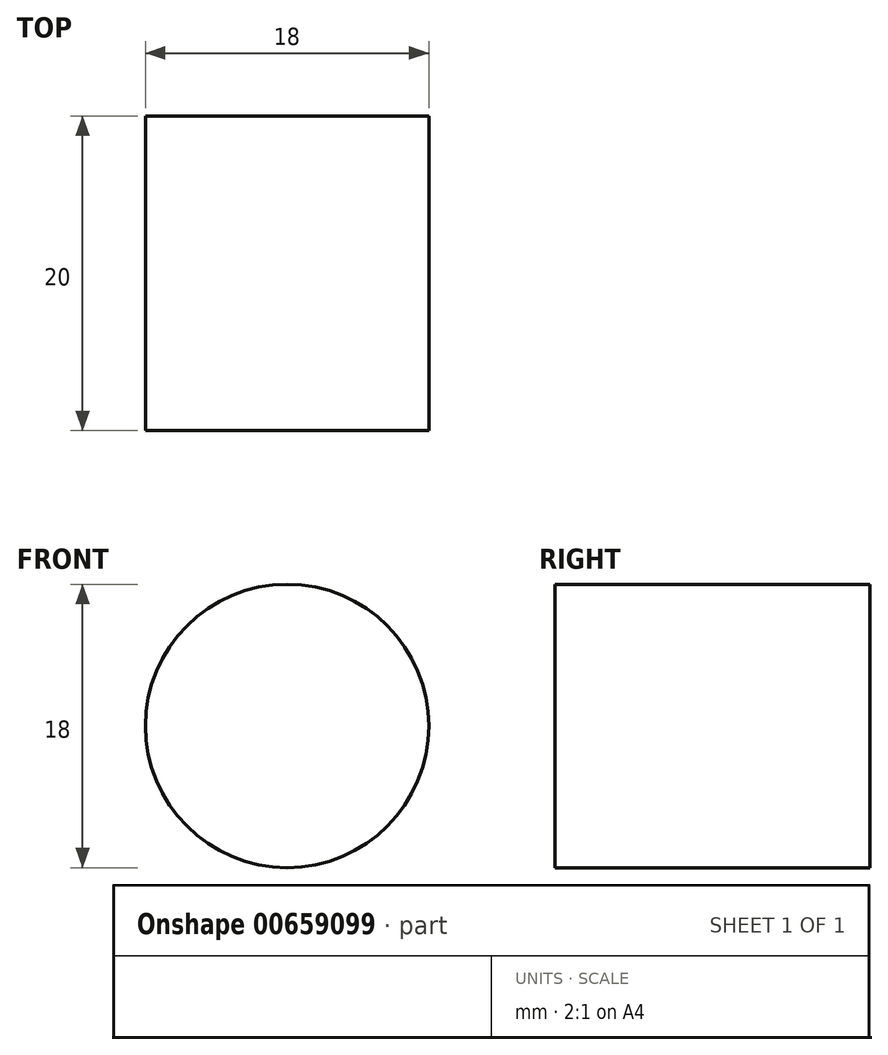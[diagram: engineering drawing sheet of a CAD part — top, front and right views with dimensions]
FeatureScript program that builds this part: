
annotation { "Feature Type Name" : "Feature", "Feature Type Description" : "" }
export const myFeature = defineFeature(function(context is Context, id is Id, definition is map)
    precondition{}
    {
        {
            var Q0;
            Q0=qCreatedBy(makeId("Front.planeOp"),FACE);
            var sketch = newSketch(context, id + "F0", { "sketchPlane" : qUnion([Q0])});
            skCircle(sketch, "E0", {"center": v(0, 0) * mm, "radius": 9 * mm});
            skSolve(sketch);
        }
        {
            var Q0;
            Q0=makeQuery(id+"F0.imprint","IMPRINT",FACE,{"disambiguationData":[TD([[makeQuery(id+"F0.imprint","IMPRINT",EDGE,{"derivedFrom":sQuery(id+"F0.wireOp",EDGE,"E0")}),1.0]])]});
            extrude(context, id + "F1", {"entities" : qUnion([Q0]), "depth" : 20 * mm, "offsetDistance" : 25.4 * mm});
        }
    });
